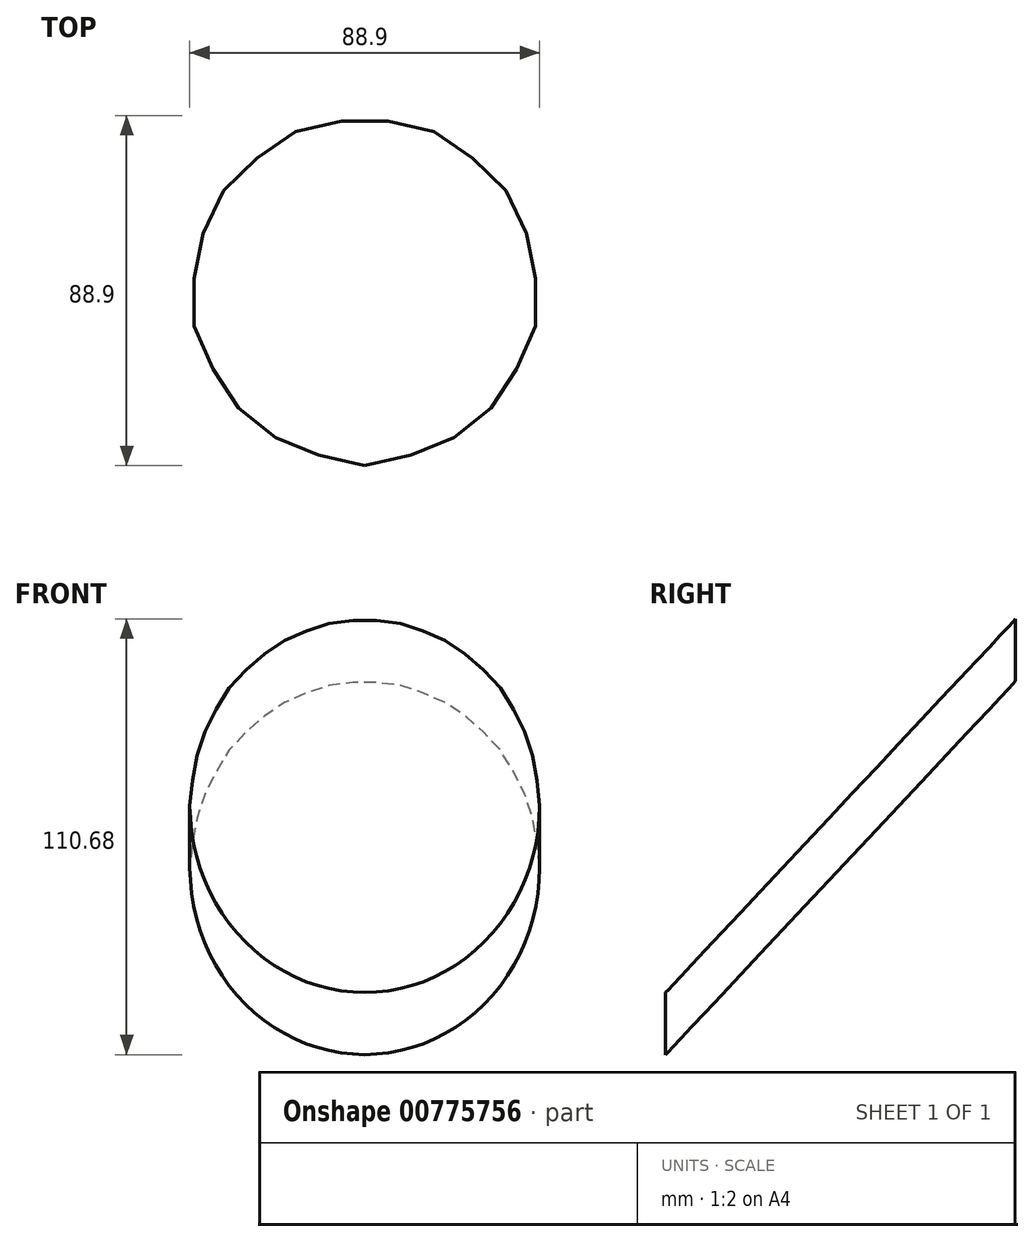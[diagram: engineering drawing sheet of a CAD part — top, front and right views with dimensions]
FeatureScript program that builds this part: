
annotation { "Feature Type Name" : "Feature", "Feature Type Description" : "" }
export const myFeature = defineFeature(function(context is Context, id is Id, definition is map)
    precondition{}
    {
        {
            var Q0;
            Q0=qCreatedBy(makeId("Top.planeOp"),FACE);
            var sketch = newSketch(context, id + "F0", { "sketchPlane" : qUnion([Q0])});
            skCircle(sketch, "E0", {"center": v(0, 0) * mm, "radius": 44.45 * mm});
            skSolve(sketch);
        }
        {
            var Q0;
            Q0 = qSketchRegion(id + "F0", true);
            extrude(context, id + "F1", {"entities" : qUnion([Q0]), "depth" : 114.04 * mm, "offsetDistance" : 25.4 * mm});
        }
        {
            var Q0;
            Q0=qCreatedBy(makeId("Right.planeOp"),FACE);
            var sketch = newSketch(context, id + "F2", { "sketchPlane" : qUnion([Q0])});
            skLineSegment(sketch, "E1", {"start": v(-45.93, 0) * mm, "end": v(45.5, 0) * mm});
            skLineSegment(sketch, "E2", {"start": v(45.5, 0) * mm, "end": v(45.5, 97.6) * mm});
            skLineSegment(sketch, "E3", {"start": v(45.5, 97.6) * mm, "end": v(-45.93, 0) * mm});
            skPoint(sketch, "E4.end.orphan", {"position": v(-45.93, 26.81) * mm});
            skLineSegment(sketch, "E5", {"start": v(-45.7, 16.03) * mm, "end": v(-45.7, 115.09) * mm});
            skLineSegment(sketch, "E6", {"start": v(-45.7, 115.09) * mm, "end": v(47.1, 115.09) * mm});
            skLineSegment(sketch, "E7", {"start": v(47.1, 115.09) * mm, "end": v(-45.7, 16.03) * mm});
            skSolve(sketch);
        }
        {
            var Q0;
            Q0 = qSketchRegion(id + "F2", true);
            extrude(context, id + "F3", {"entities" : qUnion([Q0]), "operationType" : NewBodyOperationType.REMOVE, "endBound" : BoundingType.THROUGH_ALL, "oppositeDirection" : true, "depth" : 50.8 * mm, "offsetDistance" : 25.4 * mm, "hasSecondDirection" : true, "secondDirectionOppositeDirection" : false, "secondDirectionDepth" : 50.8 * mm});
        }
    });
